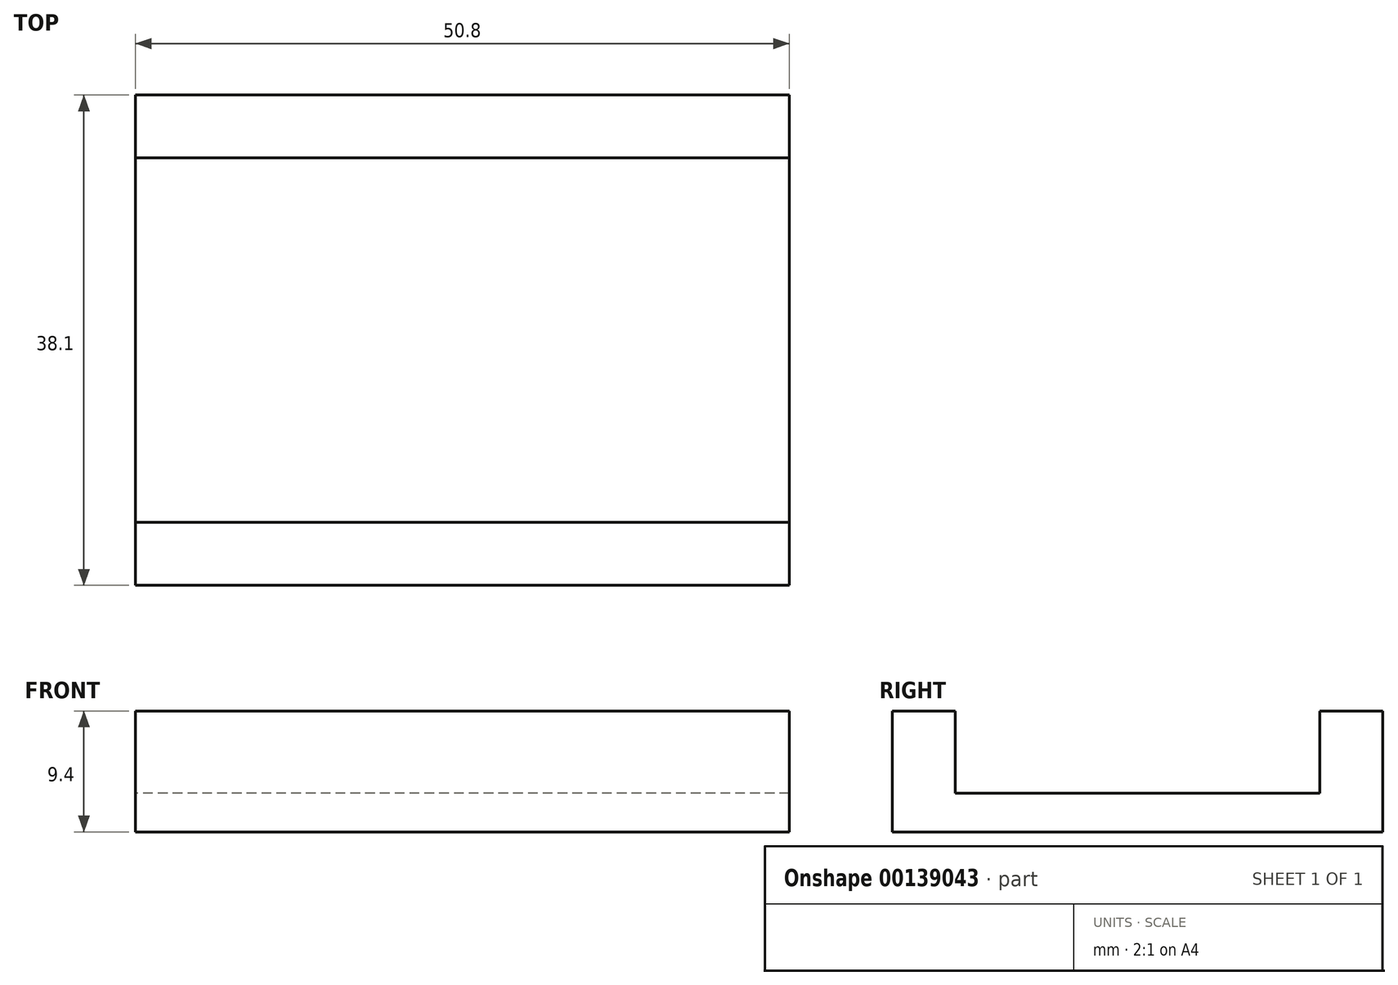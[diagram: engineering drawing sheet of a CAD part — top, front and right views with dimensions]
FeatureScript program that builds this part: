
annotation { "Feature Type Name" : "Feature", "Feature Type Description" : "" }
export const myFeature = defineFeature(function(context is Context, id is Id, definition is map)
    precondition{}
    {
        {
            var Q0;
            Q0=qCreatedBy(makeId("Right.planeOp"),FACE);
            var sketch = newSketch(context, id + "F0", { "sketchPlane" : qUnion([Q0])});
            skLineSegment(sketch, "E0.top", {"start": v(-17.82, -7.75) * mm, "end": v(20.28, -7.75) * mm});
            skLineSegment(sketch, "E0.left", {"start": v(-17.82, -4.75) * mm, "end": v(-17.82, -7.75) * mm});
            skLineSegment(sketch, "E0.right", {"start": v(20.28, -4.75) * mm, "end": v(20.28, -7.75) * mm});
            skLineSegment(sketch, "E1", {"start": v(-17.82, -4.75) * mm, "end": v(-17.82, 1.65) * mm});
            skLineSegment(sketch, "E2", {"start": v(-17.82, 1.65) * mm, "end": v(-12.92, 1.65) * mm});
            skLineSegment(sketch, "E3", {"start": v(-12.92, 1.65) * mm, "end": v(-12.92, -4.75) * mm});
            skLineSegment(sketch, "E4", {"start": v(20.28, -4.75) * mm, "end": v(20.28, 1.65) * mm});
            skLineSegment(sketch, "E5", {"start": v(20.28, 1.65) * mm, "end": v(15.4, 1.65) * mm});
            skLineSegment(sketch, "E6", {"start": v(15.4, 1.65) * mm, "end": v(15.4, -4.75) * mm});
            skLineSegment(sketch, "E7", {"start": v(15.4, -4.75) * mm, "end": v(-12.92, -4.75) * mm});
            skSolve(sketch);
        }
        {
            var Q0;
            Q0 = qSketchRegion(id + "F0", true);
            extrude(context, id + "F1", {"entities" : qUnion([Q0]), "depth" : 50.8 * mm});
        }
    });
